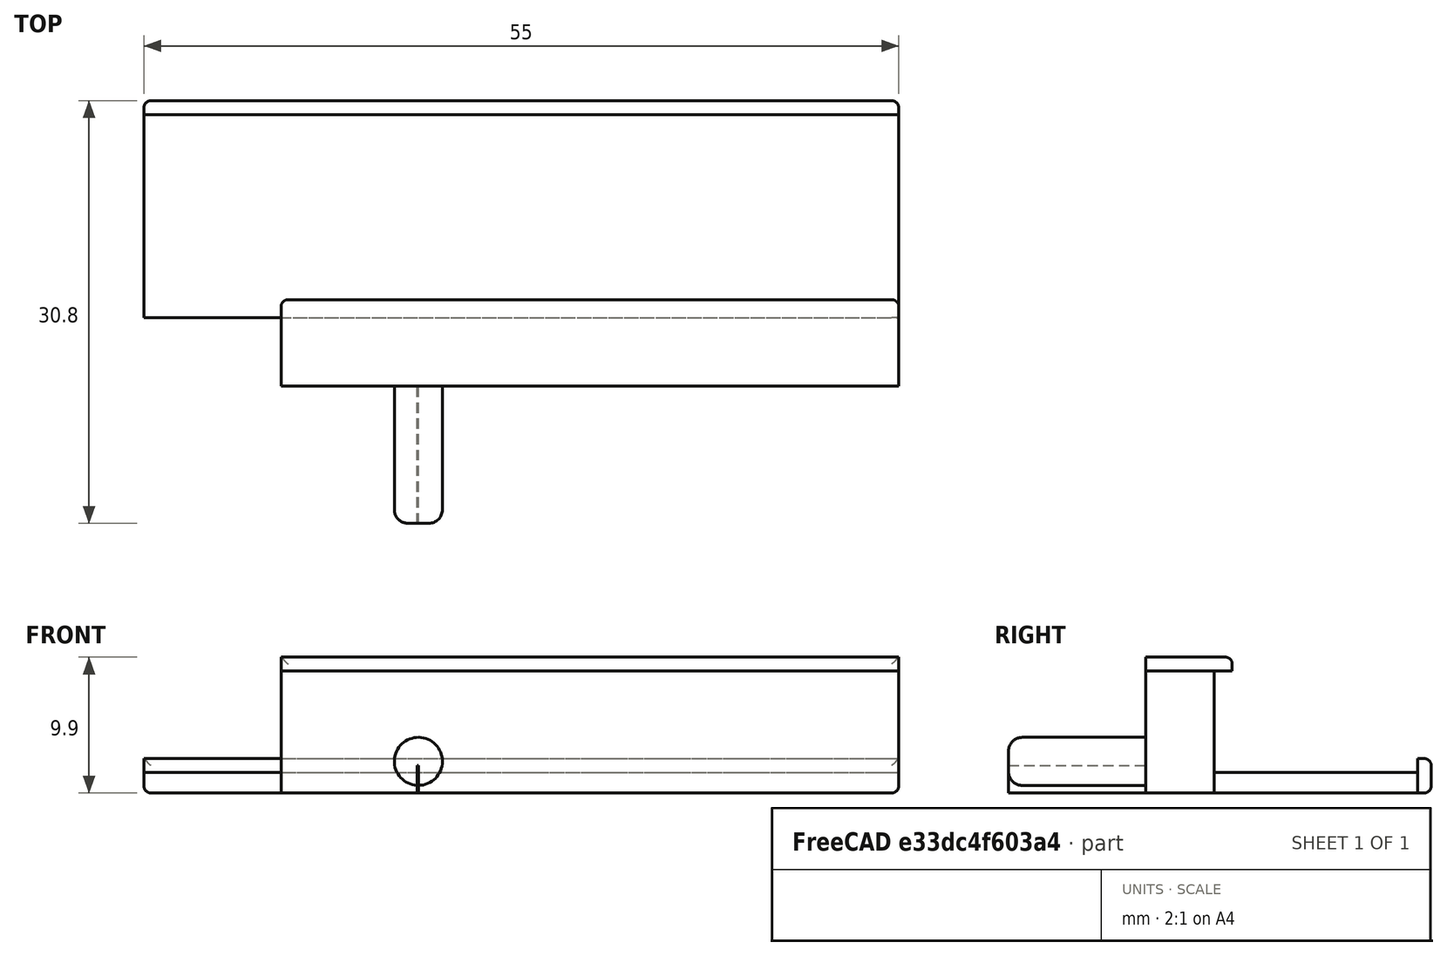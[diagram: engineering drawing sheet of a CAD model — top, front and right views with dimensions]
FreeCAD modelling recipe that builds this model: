
FCSTD DOCUMENT  (FreeCAD 0.21R33771 (Git))
Label: usb-support-3-round
License: All rights reserved
LicenseURL: http://en.wikipedia.org/wiki/All_rights_reserved
objects: Part::Box×5, Part::Fillet×5, Part::Cylinder×1
note: 11 computed .brp shape members not serialized (recipe doc carries the construction recipe); baked Part::Feature solids carry a one-line shape summary decoded from their .brp

FEATURE [Part::Box] Box  label="Cube"
  AttacherType = Attacher::AttachEngine3D
  Height = 8.9
  Length = 45
  Placement = pos=(10,0,0) rot=(0,0,1;0rad)
  Width = 5
FEATURE [Part::Box] Box001  label="Cube001"
  AttacherType = Attacher::AttachEngine3D
  Height = 1.5
  Length = 55
  Placement = pos=(0,5,0) rot=(0,0,1;0rad)
  Width = 14.8
FEATURE [Part::Box] Box002  label="Cube002"
  AttacherType = Attacher::AttachEngine3D
  Height = 2.5
  Length = 55
  Placement = pos=(0,19.8,0) rot=(0,0,1;0rad)
  Width = 1
FEATURE [Part::Box] Box003  label="Cube003"
  AttacherType = Attacher::AttachEngine3D
  Height = 1
  Length = 45
  Placement = pos=(10,0,8.9) rot=(0,0,1;0rad)
  Width = 6.3
FEATURE [Part::Cylinder] Cylinder
  Angle = 360
  AttacherType = Attacher::AttachEngine3D
  FirstAngle = 0
  Height = 10
  Placement = pos=(20,0,2.3) rot=(1,0,0;1.5708rad)
  Radius = 1.75
  SecondAngle = 0
FEATURE [Part::Fillet] Fillet
  Base = -> Cylinder
  Edges = 1 edges r=1: [Edge3]
FEATURE [Part::Fillet] Fillet001
  Base = -> Box002
  Edges = 6 edges r=0.5: [Edge3,Edge4,Edge7,Edge8,Edge11,Edge12]
FEATURE [Part::Fillet] Fillet003
  Base = -> Box001
  Edges = 2 edges r=0.5: [Edge4,Edge8]
FEATURE [Part::Fillet] Fillet004
  Base = -> Box
  Edges = 1 edges r=0.5: [Edge8]
FEATURE [Part::Fillet] Fillet005
  Base = -> Box003
  Edges = 3 edges r=0.5: [Edge3,Edge7,Edge12]
FEATURE [Part::Box] Box004  label="Cube004"
  AttacherType = Attacher::AttachEngine3D
  Height = 2
  Length = 0.1
  Placement = pos=(19.9,-10,0) rot=(0,0,1;0rad)
  Width = 10
